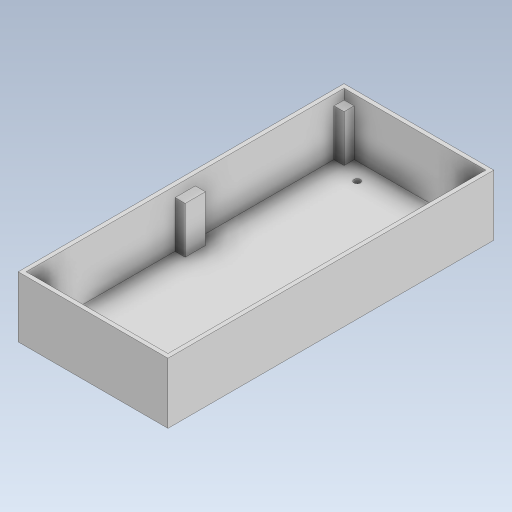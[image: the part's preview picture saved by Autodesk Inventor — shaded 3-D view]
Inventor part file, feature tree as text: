
AUTODESK INVENTOR PART (.ipt)
format: ipt  version: 2023.5 (Build 275446000, 446)  size: 181,248 bytes
history: native  units: mm
features: extrude x3, sketch x1
ambient origin geometry x8: Origin, YZ Plane, XZ Plane, XY Plane, X Axis, Y Axis, Z Axis, Center Point
bodies: Solid1 (feature_tree)
feature tree (4):
  sketch  "Sketch1"  dims[d0=70.0mm d1=157.0mm d2=74.0mm d3=161.0mm d4=3.2mm d5=17.0mm d6=70.0mm d7=5.5mm d8=3.2mm d9=5.5mm d10=34.0mm d11=5.0mm d12=5.0mm d13=5.0mm d14=5.0mm d15=5.0mm d16=5.0mm d17=5.0mm d18=2.0mm d19=0.0mm d20=25.0mm d21=0.0mm d22=30.0mm d23=0.0mm]
  extrude  "Extrusion1"  Depth=157.0mm
  extrude  "Extrusion2"  Depth=74.0mm
  extrude  "Extrusion3"  Depth=161.0mm
